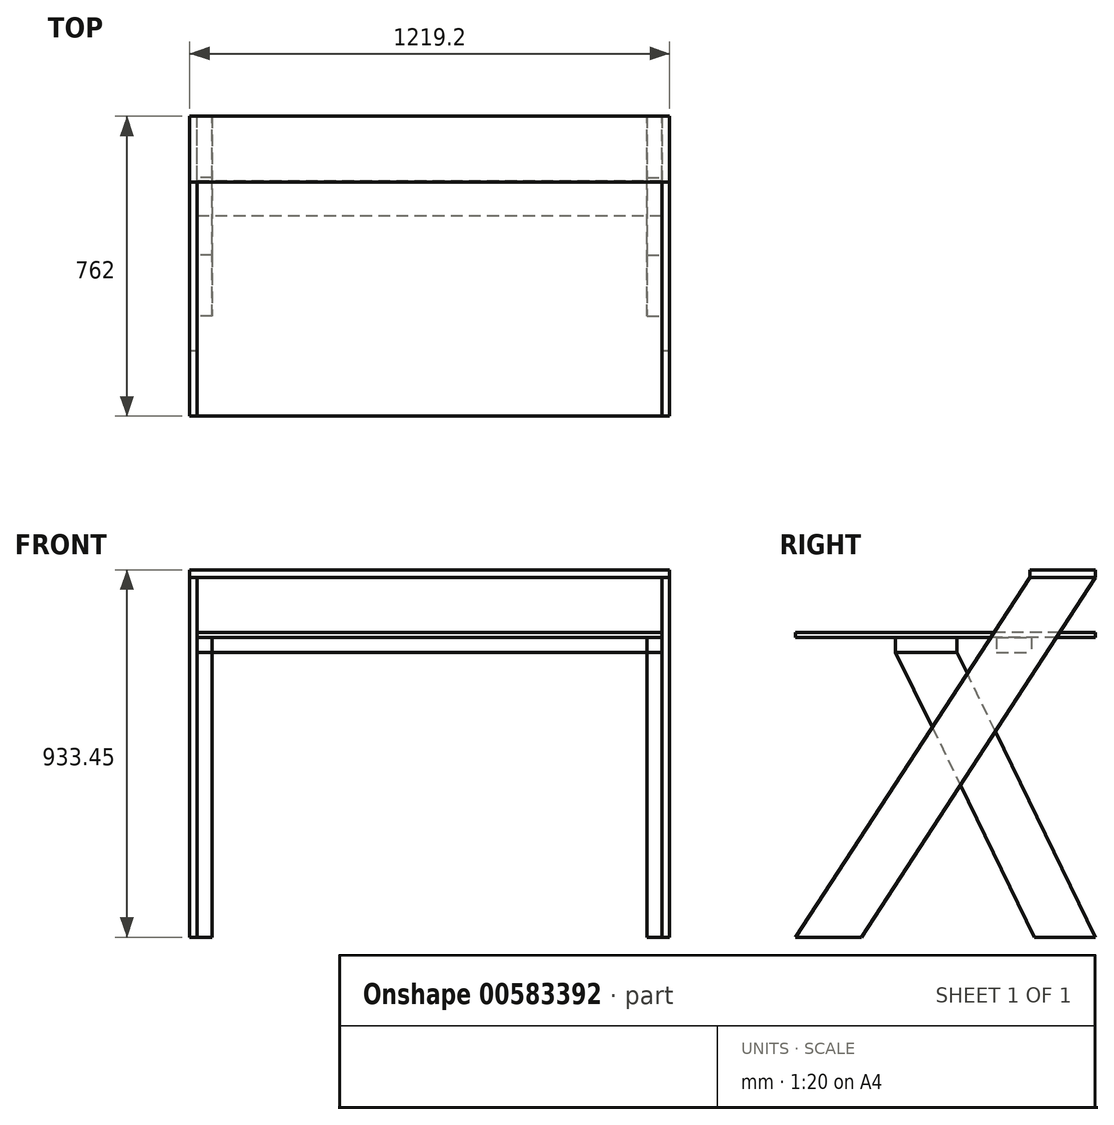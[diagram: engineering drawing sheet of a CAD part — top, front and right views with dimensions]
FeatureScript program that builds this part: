
annotation { "Feature Type Name" : "Feature", "Feature Type Description" : "" }
export const myFeature = defineFeature(function(context is Context, id is Id, definition is map)
    precondition{}
    {
        {
            var Q0;
            Q0=qCreatedBy(makeId("Top.planeOp"),FACE);
            var sketch = newSketch(context, id + "F0", { "sketchPlane" : qUnion([Q0])});
            skLineSegment(sketch, "E0.bottom", {"start": v(-609.6, -381) * mm, "end": v(-590.55, -381) * mm});
            skLineSegment(sketch, "E0.top", {"start": v(-609.6, 381) * mm, "end": v(-590.55, 381) * mm});
            skLineSegment(sketch, "E0.left", {"start": v(-609.6, -381) * mm, "end": v(-609.6, 381) * mm});
            skLineSegment(sketch, "E0.right", {"start": v(-590.55, -381) * mm, "end": v(-590.55, 381) * mm});
            skPoint(sketch, "E0.middle", {"position": v(-600.08, 0) * mm});
            skLineSegment(sketch, "E1.bottom", {"start": v(590.55, -381) * mm, "end": v(609.6, -381) * mm});
            skLineSegment(sketch, "E1.top", {"start": v(590.55, 381) * mm, "end": v(609.6, 381) * mm});
            skLineSegment(sketch, "E1.left", {"start": v(590.55, -381) * mm, "end": v(590.55, 381) * mm});
            skLineSegment(sketch, "E1.right", {"start": v(609.6, -381) * mm, "end": v(609.6, 381) * mm});
            skPoint(sketch, "E1.middle", {"position": v(600.08, 0) * mm});
            skSolve(sketch);
        }
        {
            var Q0;
            Q0 = qSketchRegion(id + "F0", true);
            extrude(context, id + "F1", {"entities" : qUnion([Q0]), "depth" : 914.4 * mm, "offsetDistance" : 25.4 * mm});
        }
        {
            var Q0;
            Q0=makeQuery(id+"F1.opExtrude","SWEPT_FACE",FACE,{"disambiguationData":[OSD([sQuery(id+"F0.wireOp",EDGE,"E1.right")])]});
            var sketch = newSketch(context, id + "F2", { "sketchPlane" : qUnion([Q0])});
            skLineSegment(sketch, "E2", {"start": v(-214.3, 0) * mm, "end": v(381, 914.4) * mm});
            skLineSegment(sketch, "E3", {"start": v(214.3, 914.4) * mm, "end": v(-381, 0) * mm});
            skLineSegment(sketch, "E4", {"start": v(-214.3, 0) * mm, "end": v(-331.38, 76.22) * mm, "construction": true});
            skLineSegment(sketch, "E5.0.0", {"start": v(-214.3, 0) * mm, "end": v(381, 0) * mm});
            skLineSegment(sketch, "E5.0.1", {"start": v(381, 0) * mm, "end": v(381, 914.4) * mm});
            skLineSegment(sketch, "E5.0.2", {"start": v(214.3, 914.4) * mm, "end": v(-381, 914.4) * mm});
            skLineSegment(sketch, "E5.0.3", {"start": v(-381, 914.4) * mm, "end": v(-381, 0) * mm});
            skSolve(sketch);
        }
        {
            var Q0;
            Q0 = qSketchRegion(id + "F2", true);
            extrude(context, id + "F3", {"entities" : qUnion([Q0]), "operationType" : NewBodyOperationType.REMOVE, "endBound" : BoundingType.THROUGH_ALL, "oppositeDirection" : true, "depth" : 25.4 * mm, "offsetDistance" : 25.4 * mm});
        }
        {
            var Q0;
            Q0=makeQuery(id+"F1.opExtrude","CAP_FACE",FACE,{"disambiguationData":[OSD([sQuery(id+"F0.wireOp",EDGE,"E0.bottom"),sQuery(id+"F0.wireOp",EDGE,"E0.top"),sQuery(id+"F0.wireOp",EDGE,"E0.left"),sQuery(id+"F0.wireOp",EDGE,"E0.right")])],"isStart":false});
            var sketch = newSketch(context, id + "F4", { "sketchPlane" : qUnion([Q0])});
            skLineSegment(sketch, "E6.bottom", {"start": v(-609.6, 214.3) * mm, "end": v(609.6, 214.3) * mm});
            skLineSegment(sketch, "E6.top", {"start": v(-609.6, 381) * mm, "end": v(609.6, 381) * mm});
            skLineSegment(sketch, "E6.left", {"start": v(-609.6, 214.3) * mm, "end": v(-609.6, 381) * mm});
            skLineSegment(sketch, "E6.right", {"start": v(609.6, 214.3) * mm, "end": v(609.6, 381) * mm});
            skPoint(sketch, "E6.middle", {"position": v(0, 297.65) * mm});
            skSolve(sketch);
        }
        {
            var Q0;
            Q0 = qSketchRegion(id + "F4", true);
            extrude(context, id + "F5", {"entities" : qUnion([Q0]), "depth" : 19.05 * mm, "offsetDistance" : 25.4 * mm});
        }
        {
            var Q0;
            Q0=makeQuery(id+"F1.opExtrude","SWEPT_FACE",FACE,{"disambiguationData":[OSD([sQuery(id+"F0.wireOp",EDGE,"E0.right")])]});
            var sketch = newSketch(context, id + "F6", { "sketchPlane" : qUnion([Q0])});
            skLineSegment(sketch, "E7", {"start": v(297.65, 914.4) * mm, "end": v(198.43, 762) * mm, "construction": true});
            skLineSegment(sketch, "E8", {"start": v(381, 0) * mm, "end": v(28.4, 723.9) * mm});
            skLineSegment(sketch, "E9", {"start": v(28.4, 723.9) * mm, "end": v(-127, 723.9) * mm});
            skLineSegment(sketch, "E10", {"start": v(-127, 723.9) * mm, "end": v(225.6, 0) * mm});
            skLineSegment(sketch, "E11", {"start": v(225.6, 0) * mm, "end": v(381, 0) * mm});
            skLineSegment(sketch, "E12", {"start": v(225.6, 0) * mm, "end": v(351.2, 61.18) * mm, "construction": true});
            skSolve(sketch);
        }
        {
            var Q0;
            Q0 = qSketchRegion(id + "F6", true);
            extrude(context, id + "F7", {"entities" : qUnion([Q0]), "depth" : 38.1 * mm, "offsetDistance" : 25.4 * mm});
        }
        {
            var Q0;
            Q0=makeQuery(id+"F7.opExtrude","SWEPT_FACE",FACE,{"disambiguationData":[OSD([sQuery(id+"F6.wireOp",EDGE,"E9")])]});
            var sketch = newSketch(context, id + "F8", { "sketchPlane" : qUnion([Q0])});
            skLineSegment(sketch, "E13.0.0", {"start": v(-590.55, 28.4) * mm, "end": v(-590.55, -127) * mm});
            skLineSegment(sketch, "E13.0.1", {"start": v(-590.55, -127) * mm, "end": v(-552.45, -127) * mm});
            skLineSegment(sketch, "E13.0.2", {"start": v(-552.45, -127) * mm, "end": v(-552.45, 28.4) * mm});
            skLineSegment(sketch, "E13.0.3", {"start": v(-552.45, 28.4) * mm, "end": v(-590.55, 28.4) * mm});
            skLineSegment(sketch, "E14.bottom", {"start": v(-590.55, 129.18) * mm, "end": v(590.55, 129.18) * mm});
            skLineSegment(sketch, "E14.top", {"start": v(-590.55, 218.08) * mm, "end": v(590.55, 218.08) * mm});
            skLineSegment(sketch, "E14.left", {"start": v(-590.55, 129.18) * mm, "end": v(-590.55, 218.08) * mm});
            skLineSegment(sketch, "E14.right", {"start": v(590.55, 129.18) * mm, "end": v(590.55, 218.08) * mm});
            skPoint(sketch, "E14.middle", {"position": v(0, 173.63) * mm});
            skLineSegment(sketch, "E15", {"start": v(-590.55, 90.28) * mm, "end": v(-590.55, 256.98) * mm, "construction": true});
            skPoint(sketch, "E16.startSnap1", {"position": v(-590.55, 173.63) * mm});
            skSolve(sketch);
        }
        {
            var Q0;
            Q0 = qSketchRegion(id + "F8", true);
            extrude(context, id + "F9", {"entities" : qUnion([Q0]), "depth" : 38.1 * mm, "offsetDistance" : 25.4 * mm});
        }
        {
            var Q0;
            Q0=makeQuery(id+"F7.opExtrude","SWEPT_BODY",BODY,{"disambiguationData":[OSD([sQuery(id+"F6.wireOp",EDGE,"E8"),sQuery(id+"F6.wireOp",EDGE,"E9"),sQuery(id+"F6.wireOp",EDGE,"E10"),sQuery(id+"F6.wireOp",EDGE,"E11")])]});
            var Q1;
            Q1=makeQuery(id+"F9.opExtrude","SWEPT_BODY",BODY,{"disambiguationData":[OSD([sQuery(id+"F8.wireOp",EDGE,"E13.0.0"),sQuery(id+"F8.wireOp",EDGE,"E13.0.1"),sQuery(id+"F8.wireOp",EDGE,"E13.0.2"),sQuery(id+"F8.wireOp",EDGE,"E13.0.3")])]});
            var Q2;
            Q2=qCreatedBy(makeId("Right.planeOp"),FACE);
            mirror(context, id + "F10", {"entities" : qUnion([Q0, Q1]), "mirrorPlane" : qUnion([Q2])});
        }
        {
            var Q0;
            Q0=makeQuery(id+"F1.opExtrude","SWEPT_FACE",FACE,{"disambiguationData":[OSD([sQuery(id+"F0.wireOp",EDGE,"E0.right")])]});
            var sketch = newSketch(context, id + "F11", { "sketchPlane" : qUnion([Q0])});
            skLineSegment(sketch, "E17.bottom", {"start": v(-381, 774.7) * mm, "end": v(381, 774.7) * mm});
            skLineSegment(sketch, "E17.top", {"start": v(-381, 762) * mm, "end": v(381, 762) * mm});
            skLineSegment(sketch, "E17.left", {"start": v(-381, 774.7) * mm, "end": v(-381, 762) * mm});
            skLineSegment(sketch, "E17.right", {"start": v(381, 774.7) * mm, "end": v(381, 762) * mm});
            skSolve(sketch);
        }
        {
            var Q0;
            Q0 = qSketchRegion(id + "F11", true);
            var Q1;
            Q1=makeQuery(id+"F1.opExtrude","SWEPT_FACE",FACE,{"disambiguationData":[OSD([sQuery(id+"F0.wireOp",EDGE,"E1.left")])]});
            extrude(context, id + "F12", {"entities" : qUnion([Q0]), "endBound" : BoundingType.UP_TO_SURFACE, "depth" : 25.4 * mm, "endBoundEntityFace" : qUnion([Q1]), "offsetDistance" : 25.4 * mm});
        }
    });
